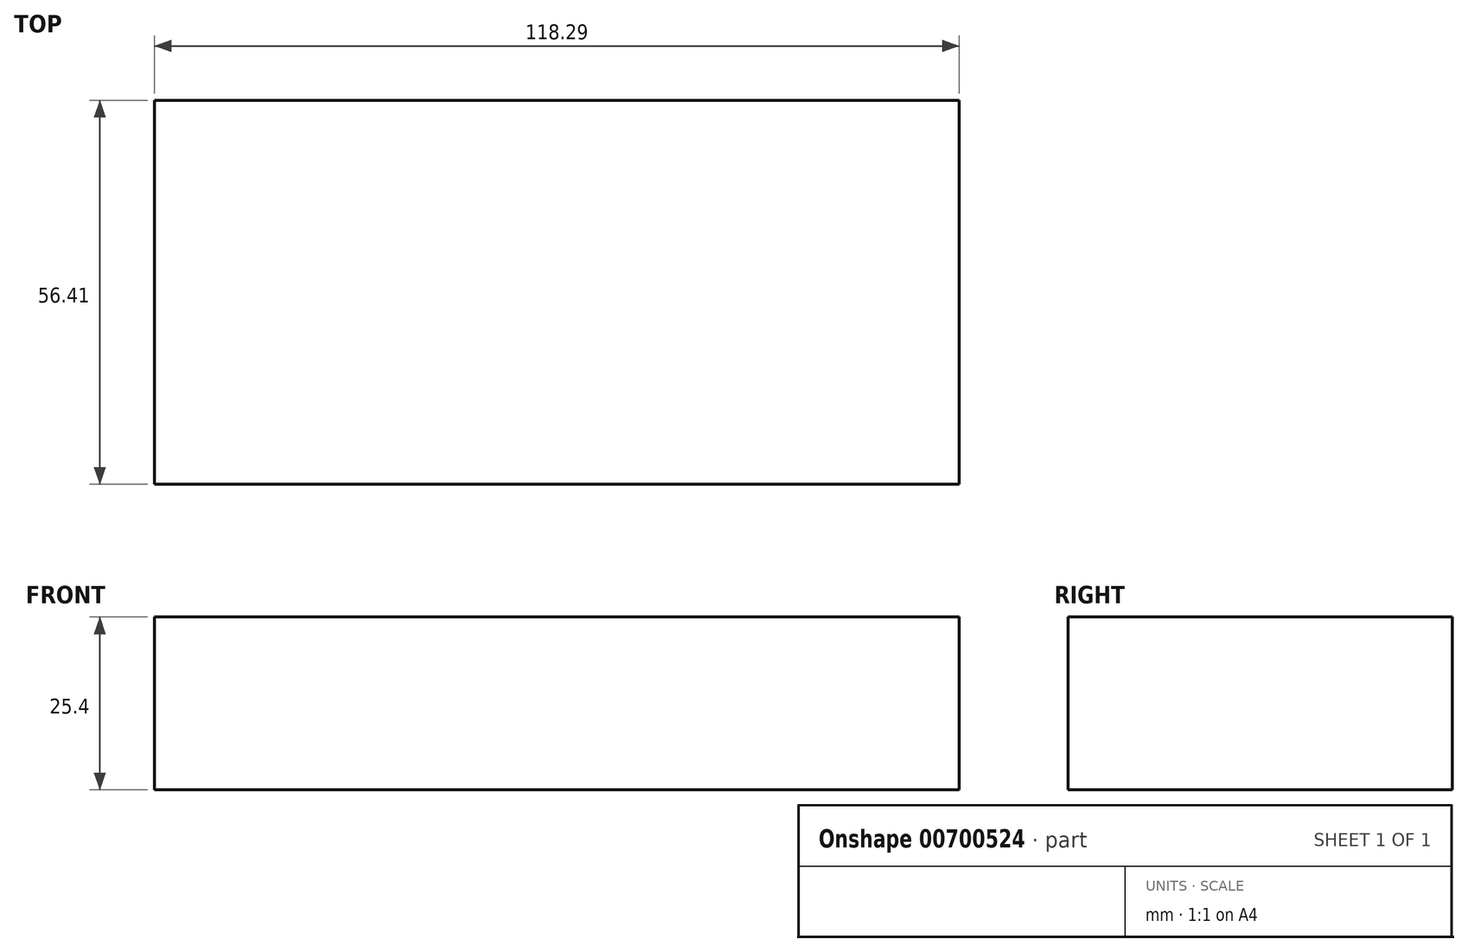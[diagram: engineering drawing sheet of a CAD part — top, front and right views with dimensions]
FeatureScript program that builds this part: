
annotation { "Feature Type Name" : "Feature", "Feature Type Description" : "" }
export const myFeature = defineFeature(function(context is Context, id is Id, definition is map)
    precondition{}
    {
        {
            var Q0;
            Q0=qCreatedBy(makeId("Top.planeOp"),FACE);
            var sketch = newSketch(context, id + "F0", { "sketchPlane" : qUnion([Q0])});
            skLineSegment(sketch, "E0.bottom", {"start": v(-53.1, 41.3) * mm, "end": v(65.19, 41.3) * mm});
            skLineSegment(sketch, "E0.top", {"start": v(-53.1, -15.1) * mm, "end": v(65.19, -15.1) * mm});
            skLineSegment(sketch, "E0.left", {"start": v(-53.1, 41.3) * mm, "end": v(-53.1, -15.1) * mm});
            skLineSegment(sketch, "E0.right", {"start": v(65.19, 41.3) * mm, "end": v(65.19, -15.1) * mm});
            skSolve(sketch);
        }
        {
            var Q0;
            Q0=makeQuery(id+"F0.imprint","IMPRINT",FACE,{"disambiguationData":[TD([[makeQuery(id+"F0.imprint","IMPRINT",EDGE,{"derivedFrom":sQuery(id+"F0.wireOp",EDGE,"E0.bottom")}),-1.0]])]});
            extrude(context, id + "F1", {"entities" : qUnion([Q0]), "depth" : 25.4 * mm, "offsetDistance" : 25.4 * mm});
        }
    });
